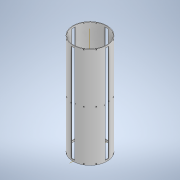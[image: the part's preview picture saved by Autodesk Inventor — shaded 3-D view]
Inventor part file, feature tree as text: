
AUTODESK INVENTOR PART (.ipt)
format: ipt  version: 2021 (Build 250183000, 183)  size: 342,016 bytes
history: native  units: in
note: dims shown in document units (in); Inventor stores cm internally (conversion verified against a paired STEP export)
features: other x26, pattern_circular x6, hole x6, sketch x5, plane x3, extrude x2
ambient origin geometry x8: Origin, YZ Plane, XZ Plane, XY Plane, X Axis, Y Axis, Z Axis, Center Point
bodies: Solid1 (feature_tree)
feature tree (48):
  extrude  "Extrusion1"  Depth=0.3937in
  plane  "Work Plane1"
  extrude  "Extrusion2"  Depth=1.5748in TaperAngle=360.0deg
  pattern_circular  "Circular Pattern1"  [2 undecoded]
  other  "Work Axis1"
  other  "Work Axis2"
  other  "Work Axis3"
  other  "Work Axis4"
  other  "Work Point1"
  other  "Work Point2"
  other  "Work Point3"
  other  "Central Plane"
  other  "Work Point4"
  other  "Work Axis6"
  other  "Work Axis7"
  other  "Offset Plane A"
  other  "Work Point5"
  other  "Work Point6"
  other  "Work Axis8"
  other  "Work Axis9"
  other  "Work Point7"
  other  "Work Point8"
  plane  "Work Plane5"
  plane  "Work Plane6"
  hole  "Hole1"  [1 undecoded]
  hole  "Hole2"  [1 undecoded]
  pattern_circular  "Circular Pattern3"  Angle=30.0deg  [1 undecoded]
  sketch  "Sketch5"  dims[d13=0.0481in]
  other  "Work Axis10"
  other  "plane for insert hole 1"
  sketch  "Sketch7"  dims[d14=-11.811in]
  other  "plane for insert hole 2"
  sketch  "Sketch8"  dims[d15=0.0481in d16=0.1574in d17=-0.1574in d48=1.0in d49=1.0in d29=0.096in d30=0.75in d31=0.185in d32=0.25in d33=0.5635in d34=1.0in d35=0.0in d52=1.0in d53=1.0in d38=0.096in d39=0.75in d40=0.185in d41=0.25in d42=0.5635in d43=1.0in d44=0.8108in d45=1.5748in d46=360.0deg d88=30.0deg d89=30.0deg d90=0.0in d91=0.0in d92=0.0in d93=11.811in d94=0.0in d95=11.811in d96=0.129in d97=0.224in d98=0.225in d99=0.25in d100=0.5635in d101=0.349in d102=0.8108in d103=0.129in d104=0.224in d105=0.225in d106=0.25in d107=0.5635in d108=0.349in d109=0.8108in d110=1.5748in d111=360.0deg d116=1.5748in d117=360.0deg d119=0.0in d120=0.0in d121=0.0in d122=0.1969in d123=0.1969in d124=0.0in d125=0.0in d126=0.1969in d127=0.1969in d128=0.129in d129=0.75in d130=0.225in d131=0.25in d132=0.5635in d133=0.349in d134=0.8108in d135=0.129in d136=0.75in d137=0.225in d138=0.25in d139=0.5635in d140=0.349in d141=0.8108in d142=1.5748in d143=360.0deg d145=1.5748in d146=360.0deg d148=22.8346in d149=-0.1969in d150=-0.1969in d54=1.0in d55=1.0in d56=1.0in d57=0.15in d58=0.25in d59=0.375in d60=0.5635in d61=0.75in d62=0.8108in d63=0.0625in d64=0.75in d65=0.375in]
  hole  "insert hole 2"  [1 undecoded]
  hole  "insert hole 1"  [1 undecoded]
  pattern_circular  "Circular Pattern7"  [2 undecoded]
  pattern_circular  "Circular Pattern9"  [2 undecoded]
  other  "Work Axis14"
  hole  "Hole8"  [1 undecoded]
  hole  "Hole9"  [1 undecoded]
  pattern_circular  "Circular Pattern10"  Count=30  [1 undecoded]
  pattern_circular  "Circular Pattern11"  Count=4 Angle=360.0deg
  other  "Edge Hole Plane 1"
  other  "Edge Hole Plane 2"
  sketch  "Sketch1"  dims[d3=0.0in d7=0.3937in]
  sketch  "Sketch2"  dims[d8=0.5in d9=0.0in d10=1.5748in d11=360.0deg]
  other  "Work Axis5"
  other  "Offset Plane B"
note: 14 required parameter values undecoded (feature->parameter linkage not recoverable at this tier; creation-order binding heuristic only, values carry confidence <= 0.55)
